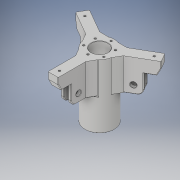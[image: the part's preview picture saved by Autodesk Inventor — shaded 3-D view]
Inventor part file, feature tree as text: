
AUTODESK INVENTOR PART (.ipt)
format: ipt  version: 2019 (Build 230136000, 136)  size: 394,752 bytes
history: native  units: mm
features: sketch x5, extrude x3, chamfer x3, projected_geometry x2, other x1, pattern_circular x1, hole x1
ambient origin geometry x8: Origin, YZ Plane, XZ Plane, XY Plane, X Axis, Y Axis, Z Axis, Center Point
bodies: Solide1 (feature_tree)
feature tree (16):
  other  "Révolution1"
  extrude  "Extrusion3"  Depth=0.5mm
  extrude  "Extrusion4"  Depth=0.5mm
  chamfer  "Chanfrein2"  Distance=0.5mm
  chamfer  "Chanfrein4"  Distance=0.5mm
  extrude  "Extrusion5"  Depth=100.0mm
  chamfer  "Chanfrein5"  Distance=0.5mm
  pattern_circular  "Réseau circulaire2"  [2 undecoded]
  hole  "Perçage2"  [1 undecoded]
  sketch  "Esquisse2"
  sketch  "Esquisse6"
  projected_geometry  "Boucle projetée3"
  sketch  "Esquisse8"
  sketch  "Esquisse9"
  projected_geometry  "Boucle projetée4"
  sketch  "Esquisse11"
note: 3 required parameter values undecoded (feature->parameter linkage not recoverable at this tier; creation-order binding heuristic only, values carry confidence <= 0.55)
